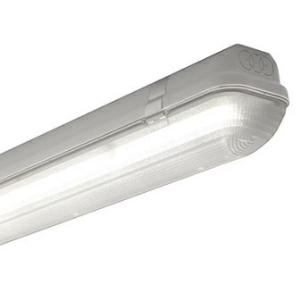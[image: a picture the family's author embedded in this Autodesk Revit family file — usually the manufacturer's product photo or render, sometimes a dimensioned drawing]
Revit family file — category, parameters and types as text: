
# Revit family: 3f_filippi_-_3f_linda_3f_filippi_-_58583_-_3f_linda_led_1x24w_l1270
name_source: partatom
category: Lighting Fixtures
units: mm (PartAtom-declared; Revit-internal decimal feet)

## family parameters
Cut with Voids When Loaded = No
Host = Face
Light Source = No
Part Type = Normal
Room Calculation Point = No
Round Connector Dimension = Use Diameter
Shared = No

## types (1)
- 3F Filippi - 3F Linda (1 x LED, 4065 lm, 28 W, 4000 K)
    Apparent Load = 28 VA
    Approval mark = CE
    CIE Flux Codes = 44 77 94 97 100
    Color Rendering = 80
    Color Temperature = 4000 K
    Control Gear = Electronic ballast
    Default Elevation = 1800 mm
    Description = ILLUMINOTECHNICAL
Luminous efficiency 100% (DLOR 97%, ULOR 3%).
Initial luminous flux of the luminaire 4065 lm.
Controlled symmetric distribution.
Installation Interdistance Transv.D = 1.77 x hu - Long.D = 1.17 x hu.
Tabular UGR (CIE 117 - 4H-8H; S=0.25H; 70/50/20): RUG 22 - 22.9.
Beam angle: 109° - 64°.
Luminous efficacy 145 lm/W.
Lifetime (L93/B10): 30000 h. (tq+25°C)
Lifetime (L90/B10): 50000 h. (tq+25°C)
Lifetime (L85/B10): 80000 h. (tq+25°C)
Lifetime (L80/B10): 100000 h. (tq+25°C)
Lifetime (L85/B10): 50000 h. (tq+35°C)
Sudden decreased luminous flux after 50000 hours: 0% (C0).
Photobiological safety in compliance with IEC/TR 62778: RG0 risk exempt, (IEC 62471).
In compliance with IEC/EN 62722-2-1 - IEC/EN 62717 standards.

SOURCE
Linear LED module 24W/840.
Energy efficiency class (UE 2019/2020 - UE 2019/2015): D.
CIE 13.3 Colour rendering index: CRI >80 (R9 <50%).
IES TM-30 Fidelity Index: Rf = 84 Rg = 95.
CCT nominal colour temperature 4000 K.
Colour initial tolerance (MacAdam): SDCM 3.

MECHANICAL
Self-extinguishing V2 polycarbonate housing, injection moulded, RAL 7035 grey.
Ecologic anti-aging injected sealing gasket.
Diffuser in self-extinguishing V2 polycarbonate, photo-engraved interior, UV stabilised, injection moulded with smooth outer surface, tamper-proof opening.
Gear-holder reflector in hot-dip galvanised steel, painted with white polyester base.
Snug fit safety snap-lock clips for diffuser mounting in stainless steel, screwdriver opening.
Fixing brackets in stainless steel.
Possibility for technicians to access the interior of the luminaire.
Luminaire with limited surface temperature. - D - (EN 60598-2-24)
Dimensions: 1270x100 mm, height 100 mm. Weight 2.059 kg.
IP66 protection degree.
Mechanical strength to impacts IK10 (20 joule).
Glow-wire test resistance 850°C.

ELECTRICAL
Halogen Free electronic wiring 230V-50/60Hz, power factor 0.90, THD <25%, constant output current, SELV, class I, 1 driver.
Power of the luminaire 28 W.
ENEC - CE.
SAFE FLICKER: PstLM=<1 and SVM=<0.4 (IEC TR 61547-1 and IEC TR 63158), to ensure a more comfortable and safe light.
Luminaire compliant with EN 60598-2-22 for power supply from a centralised emergency system CPSS (Central Power Supply System), not incorporated in the luminaire - high risk areas excluded. The default power and flux are 100% in AC and 100% in DC.
Ambient temperature from -20°C to +35°C.
Temperature class T6 max 85°C.
Relative humidity UR: <85%.

INSTALLATION
Ceiling / Suspended / Wall.
All accessories dedicated to this product are available on the Catalog and on our website www.3F-Filippi.com.

APPLICATIONS
Suitable product for food production plants (HACCP), IFS (Food Version 6), BRC (GSFS Food Version 7).
Dry, dusty indoor environments, subject to occasional water splashes.
Virtually shatterproof polycarbonate compatibly with the fumes / atmospheres that compromise the elasticity of plastic materials.
Not suitable for installation on surfaces subject to important vibrations, exposed to weather conditions, on ropes or poles.
Suitable for illumination of public car parks and parking grounds referred to DIN 67528:2018-04.

WARNING
Fixture not suitable for cold stores with an ambient temperature <0°C and/or relative humidity >85%.
Luminaire designed for disposal/recycling at end-of-life.
Replaceable (LED only) light source by a professional. Replaceable control gear by a professional.
    Height = 100 mm  [stored 0.328084 ft]
    Lamp = 1 x LED
    Lamp Light Flux = 4065 lm
    Lamp Power = 28 W
    Lamp count = 1
    Length = 1270 mm
    Lifetime = 50000 h
    Luminous efficacy = 145 lm/W
    Manufacturer = 3F Filippi
    ModVariant = No
    Model = 3F Filippi - 58583 - 3F Linda LED 1x24W L1270
    Mounting Place = Ceiling
    Mounting Type = Pendant
    Number of Poles = 1
    OnlyDefault = Yes
    Power Factor = 1
    Product Name = 3F Filippi - 3F Linda
    Product group = pendant luminaire
    ProductGroupID = 9
    Protection Class = Protection class I
    Protection Degree = IP 66
    RLX_Detail_Level = 1
    RLX_Emergency_Light_Flux = 0 lm
    RLX_Emergency_Type = 0
    RLX_Emergency_Type_DB = No
    RlxData = <blob elided: 68893 chars, md5=28e82ed0>
    Socket = socket
    Standby Power = 0 W
    System Light Flux = 4065 lm
    System Power = 28 W
    Type Comments = Product without accessories
    Type Image = 3ffilippi_3f_linda_led_1x.jpg
    URL = http://relux.com
    VarID = ---
    Voltage = 0 V
    Weight = 0.00 kg
    Width = 100 mm  [stored 0.328084 ft]

note: [stored X ft] marks values corroborated as IEEE doubles in the binary element streams (Revit-internal decimal feet)

## geometry (parser evidence)
native form markers: Blend x4, Sweep x9
no freeform markers — native parametric forms only
